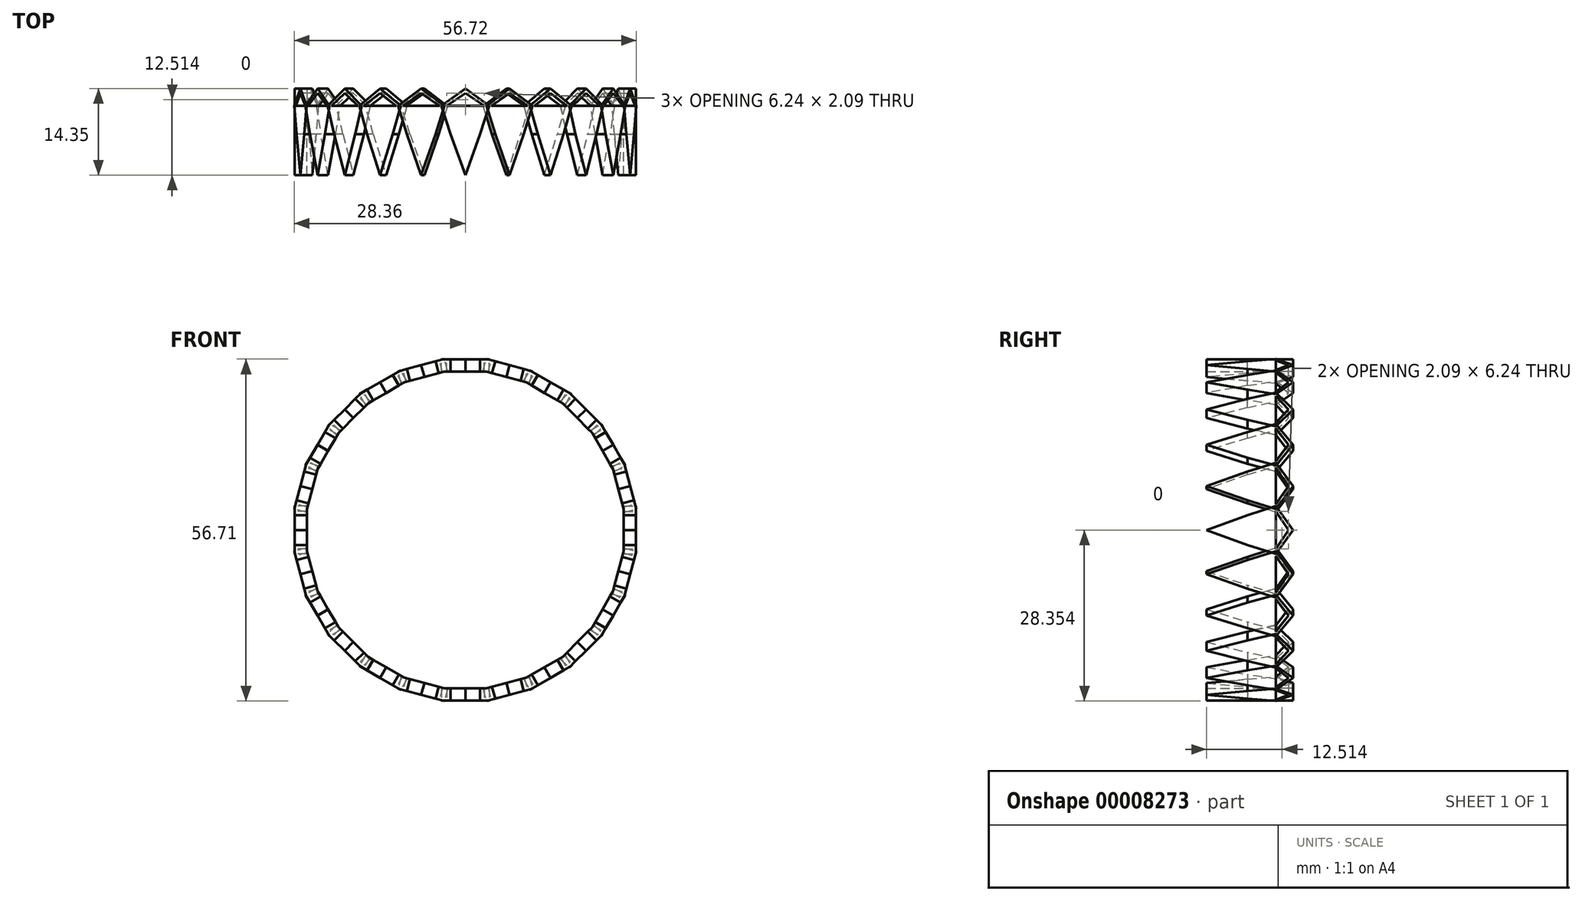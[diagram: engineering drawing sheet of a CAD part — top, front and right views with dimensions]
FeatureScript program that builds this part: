
annotation { "Feature Type Name" : "Feature", "Feature Type Description" : "" }
export const myFeature = defineFeature(function(context is Context, id is Id, definition is map)
    precondition{}
    {
        {
            var Q0;
            Q0=qCreatedBy(makeId("Top.planeOp"),FACE);
            var sketch = newSketch(context, id + "F0", { "sketchPlane" : qUnion([Q0])});
            skCircle(sketch, "E0.cCircle", {"center": v(0, 0) * mm, "radius": 3.38 * mm, "construction": true});
            skLineSegment(sketch, "E0.0", {"start": v(0, 4.17) * mm, "end": v(3.97, 1.3) * mm});
            skLineSegment(sketch, "E0.1", {"start": v(3.97, 1.3) * mm, "end": v(2.45, -3.38) * mm});
            skLineSegment(sketch, "E0.2", {"start": v(2.45, -3.38) * mm, "end": v(-2.45, -3.38) * mm});
            skLineSegment(sketch, "E0.3", {"start": v(-2.45, -3.38) * mm, "end": v(-3.97, 1.3) * mm});
            skLineSegment(sketch, "E0.4", {"start": v(-3.97, 1.3) * mm, "end": v(0, 4.17) * mm});
            skPoint(sketch, "E0.0.midPoint", {"position": v(1.99, 2.73) * mm});
            skLineSegment(sketch, "E1", {"start": v(-2.45, -3.38) * mm, "end": v(0, -10.18) * mm});
            skLineSegment(sketch, "E2", {"start": v(0, -10.18) * mm, "end": v(2.45, -3.38) * mm});
            skLineSegment(sketch, "E3", {"start": v(0, 3.38) * mm, "end": v(-3.12, 1.3) * mm});
            skLineSegment(sketch, "E4", {"start": v(-3.12, 1.3) * mm, "end": v(3.12, 1.3) * mm});
            skLineSegment(sketch, "E5", {"start": v(3.12, 1.3) * mm, "end": v(0, 3.38) * mm});
            skSolve(sketch);
        }
        {
            var Q0;
            Q0=makeQuery(id+"F0.imprint","IMPRINT",FACE,{"disambiguationData":[TD([[makeQuery(id+"F0.imprint","IMPRINT",EDGE,{"derivedFrom":sQuery(id+"F0.wireOp",EDGE,"E0.2")}),1.0]])]});
            var Q1;
            Q1=makeQuery(id+"F0.imprint","IMPRINT",FACE,{"disambiguationData":[TD([[makeQuery(id+"F0.imprint","IMPRINT",EDGE,{"derivedFrom":sQuery(id+"F0.wireOp",EDGE,"E0.0")}),-1.0]])]});
            extrude(context, id + "F1", {"entities" : qUnion([Q0, Q1]), "oppositeDirection" : true, "depth" : 2.03 * mm});
        }
        {
            var Q0;
            Q0=qCreatedBy(makeId("Right.planeOp"),FACE);
            var sketch = newSketch(context, id + "F2", { "sketchPlane" : qUnion([Q0])});
            skLineSegment(sketch, "E6", {"start": v(36.08, -28.3) * mm, "end": v(76.98, -28.3) * mm});
            skSolve(sketch);
        }
        {
            var Q0;
            Q0=makeQuery(id+"F1.opExtrude","SWEPT_BODY",BODY,{"disambiguationData":[OSD([sQuery(id+"F0.wireOp",EDGE,"E0.0"),sQuery(id+"F0.wireOp",EDGE,"E0.1"),sQuery(id+"F0.wireOp",EDGE,"E0.3"),sQuery(id+"F0.wireOp",EDGE,"E0.4"),sQuery(id+"F0.wireOp",EDGE,"E1"),sQuery(id+"F0.wireOp",EDGE,"E2"),sQuery(id+"F0.wireOp",EDGE,"E3"),sQuery(id+"F0.wireOp",EDGE,"E4"),sQuery(id+"F0.wireOp",EDGE,"E5")])]});
            var Q1;
            Q1=sQuery(id+"F2.wireOp",EDGE,"E6");
            circularPattern(context, id + "F3", {"entities" : qUnion([Q0]), "axis" : qUnion([Q1]), "angle" : 15 * degree, "instanceCount" : 30});
        }
    });
